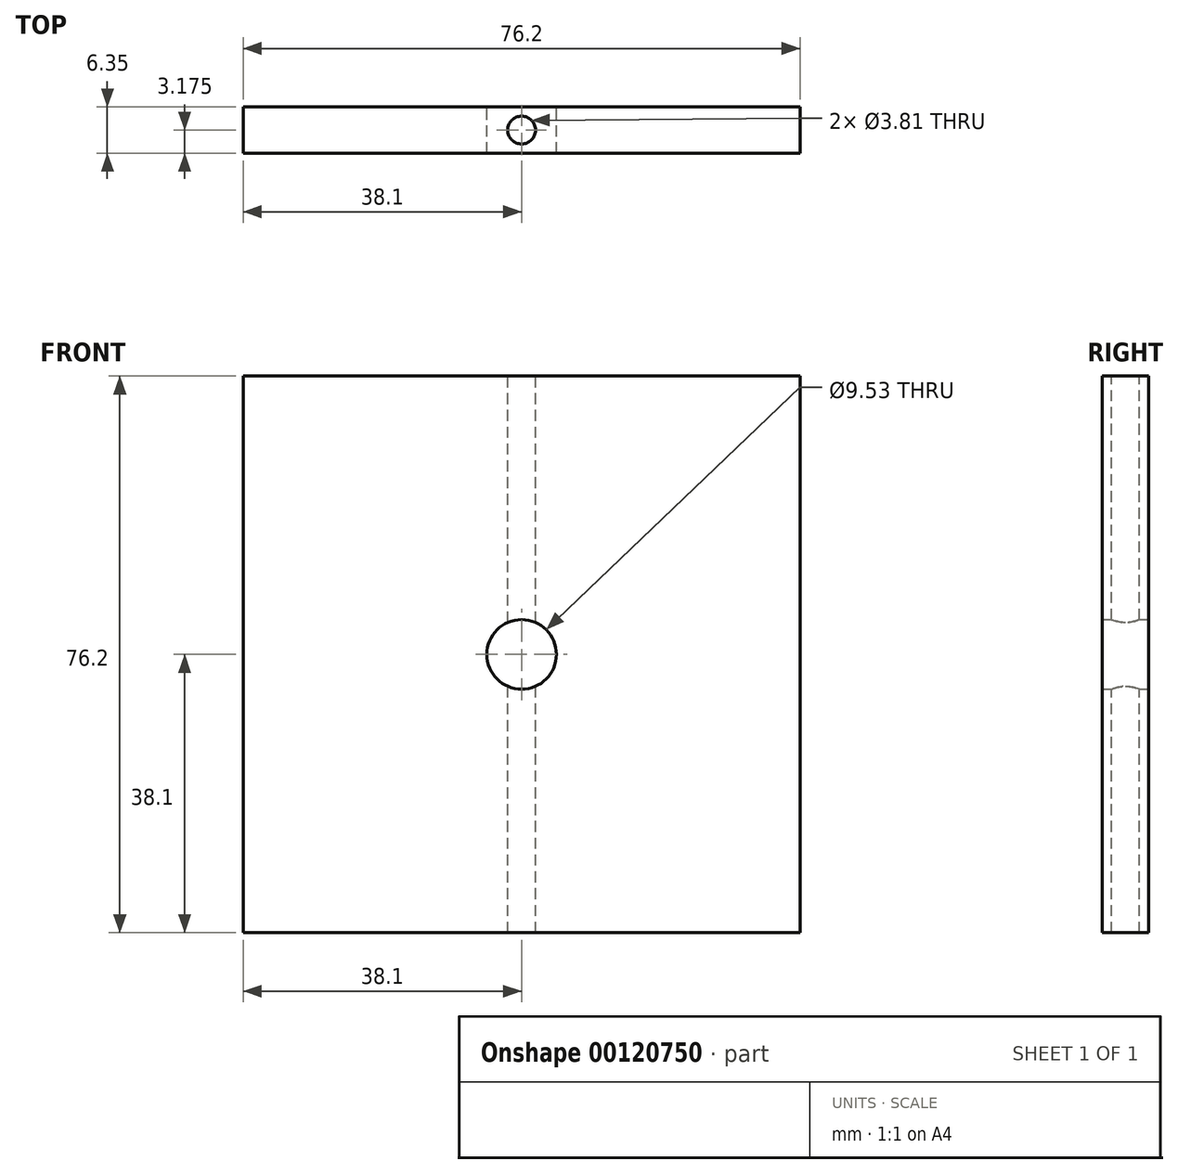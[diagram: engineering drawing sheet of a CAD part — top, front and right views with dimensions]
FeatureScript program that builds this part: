
annotation { "Feature Type Name" : "Feature", "Feature Type Description" : "" }
export const myFeature = defineFeature(function(context is Context, id is Id, definition is map)
    precondition{}
    {
        {
            var Q0;
            Q0=qCreatedBy(makeId("Front.planeOp"),FACE);
            var sketch = newSketch(context, id + "F0", { "sketchPlane" : qUnion([Q0])});
            skLineSegment(sketch, "E0.bottom", {"start": v(38.1, -38.1) * mm, "end": v(-38.1, -38.1) * mm});
            skLineSegment(sketch, "E0.top", {"start": v(38.1, 38.1) * mm, "end": v(-38.1, 38.1) * mm});
            skLineSegment(sketch, "E0.left", {"start": v(38.1, -38.1) * mm, "end": v(38.1, 38.1) * mm});
            skLineSegment(sketch, "E0.right", {"start": v(-38.1, -38.1) * mm, "end": v(-38.1, 38.1) * mm});
            skPoint(sketch, "E0.middle", {"position": v(0, 0) * mm});
            skCircle(sketch, "E1", {"center": v(0, 0) * mm, "radius": 4.76 * mm});
            skLineSegment(sketch, "E2", {"start": v(0, -38.1) * mm, "end": v(0, 38.1) * mm, "construction": true});
            skLineSegment(sketch, "E3", {"start": v(-38.1, 0) * mm, "end": v(38.1, 0) * mm, "construction": true});
            skSolve(sketch);
        }
        {
            var Q0;
            Q0 = qSketchRegion(id + "F0", true);
            extrude(context, id + "F1", {"entities" : qUnion([Q0]), "depth" : 6.35 * mm});
        }
        {
            var Q0;
            Q0=makeQuery(id+"F1.opExtrude","SWEPT_FACE",FACE,{"disambiguationData":[OSD([sQuery(id+"F0.wireOp",EDGE,"E0.top")])]});
            var sketch = newSketch(context, id + "F2", { "sketchPlane" : qUnion([Q0])});
            skCircle(sketch, "E4", {"center": v(0, -3.18) * mm, "radius": 1.9 * mm});
            skLineSegment(sketch, "E5", {"start": v(-38.1, -3.18) * mm, "end": v(38.1, -3.18) * mm, "construction": true});
            skSolve(sketch);
        }
        {
            var Q0;
            Q0 = qSketchRegion(id + "F2", true);
            extrude(context, id + "F3", {"entities" : qUnion([Q0]), "operationType" : NewBodyOperationType.REMOVE, "endBound" : BoundingType.THROUGH_ALL, "oppositeDirection" : true, "depth" : 25.4 * mm});
        }
    });
